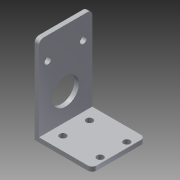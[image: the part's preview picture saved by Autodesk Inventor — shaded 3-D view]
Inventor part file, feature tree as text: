
AUTODESK INVENTOR PART (.ipt)
format: ipt  version: 2013 (Build 170138000, 138)  size: 130,560 bytes
history: native  units: in
note: dims shown in document units (in); Inventor stores cm internally (conversion verified against a paired STEP export)
features: extrude x3, sketch x3, fillet x1
ambient origin geometry x8: Origin, YZ Plane, XZ Plane, XY Plane, X Axis, Y Axis, Z Axis, Center Point
bodies: Solid1 (feature_tree)
feature tree (7):
  extrude  "Extrusion1"  Depth=2.5in
  extrude  "Extrusion2"  Depth=1.5in TaperAngle=0.0deg
  extrude  "Extrusion3"  Depth=0.625in
  fillet  "Fillet1"  Radius=0.1875in
  sketch  "Sketch1"  dims[d0=2.0in d1=2.5in]
  sketch  "Sketch2"  dims[d2=0.125in d3=1.5in d4=0.0in]
  sketch  "Sketch3"  dims[d5=1.0in d6=0.625in d7=0.1875in d8=0.1875in d9=1.5in d10=0.0in d11=0.75in d12=0.875in d13=0.75in d17=0.1875in d18=0.425in d19=1.0in d20=0.0in d21=1.625in d22=0.7874in d24=1.05in d25=0.3937in d27=1.0in d29=0.125in]
